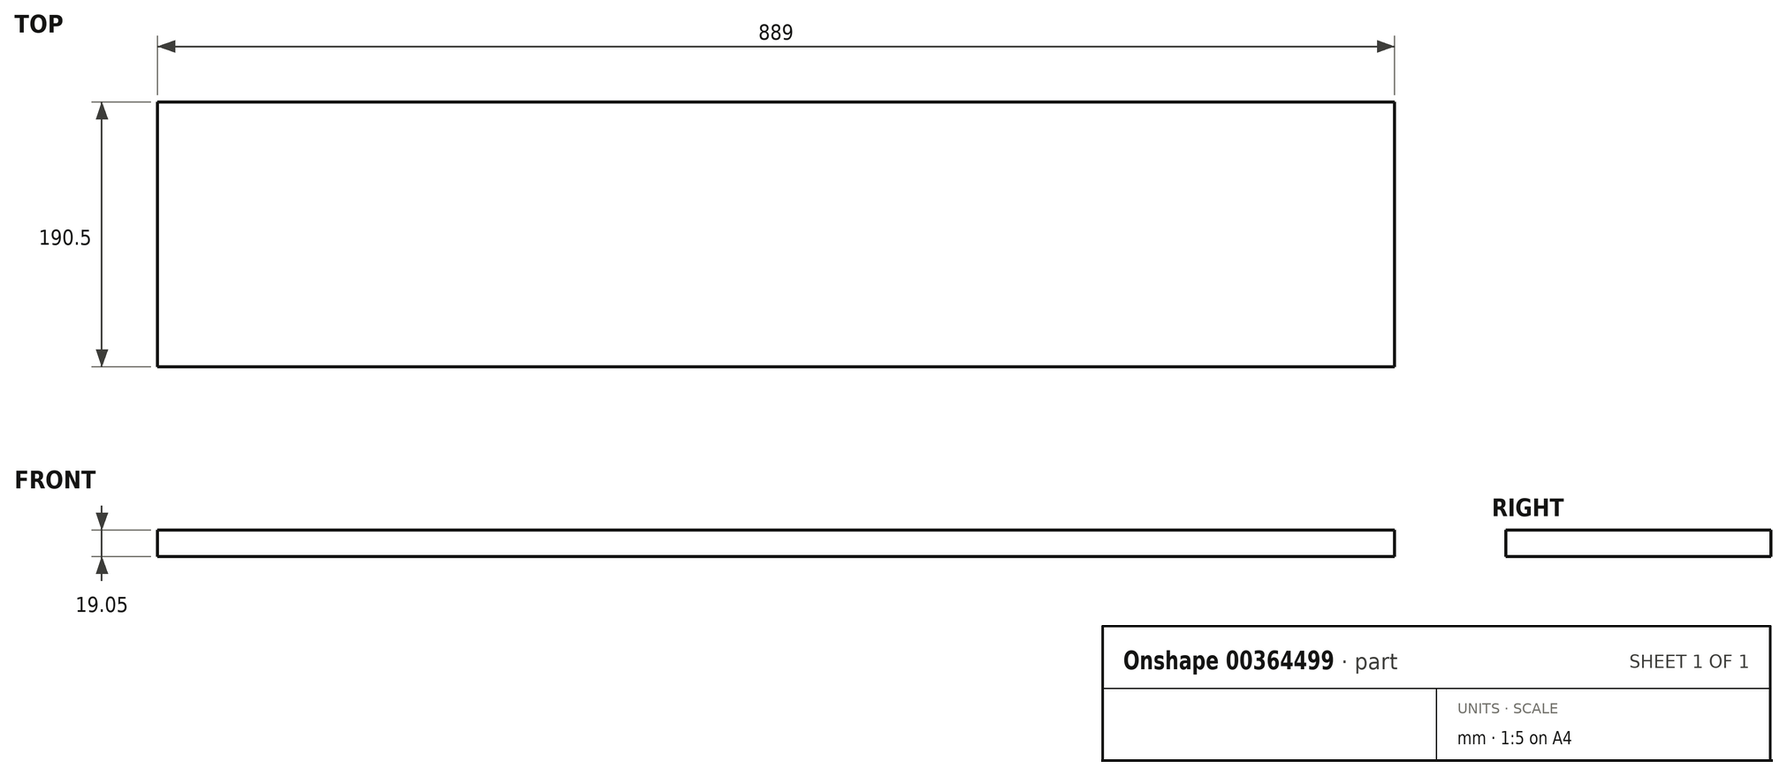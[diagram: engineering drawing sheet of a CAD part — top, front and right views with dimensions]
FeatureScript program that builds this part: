
annotation { "Feature Type Name" : "Feature", "Feature Type Description" : "" }
export const myFeature = defineFeature(function(context is Context, id is Id, definition is map)
    precondition{}
    {
        {
            var Q0;
            Q0=qCreatedBy(makeId("Top.planeOp"),FACE);
            var sketch = newSketch(context, id + "F0", { "sketchPlane" : qUnion([Q0])});
            skLineSegment(sketch, "E0.bottom", {"start": v(0, 0) * mm, "end": v(889, 0) * mm});
            skLineSegment(sketch, "E0.top", {"start": v(0, 190.5) * mm, "end": v(889, 190.5) * mm});
            skLineSegment(sketch, "E0.left", {"start": v(0, 0) * mm, "end": v(0, 190.5) * mm});
            skLineSegment(sketch, "E0.right", {"start": v(889, 0) * mm, "end": v(889, 190.5) * mm});
            skSolve(sketch);
        }
        {
            var Q0;
            Q0=qSketchRegion(id+"F0",true);
            extrude(context, id + "F1", {"entities" : qUnion([Q0]), "depth" : 19.05 * mm});
        }
    });
